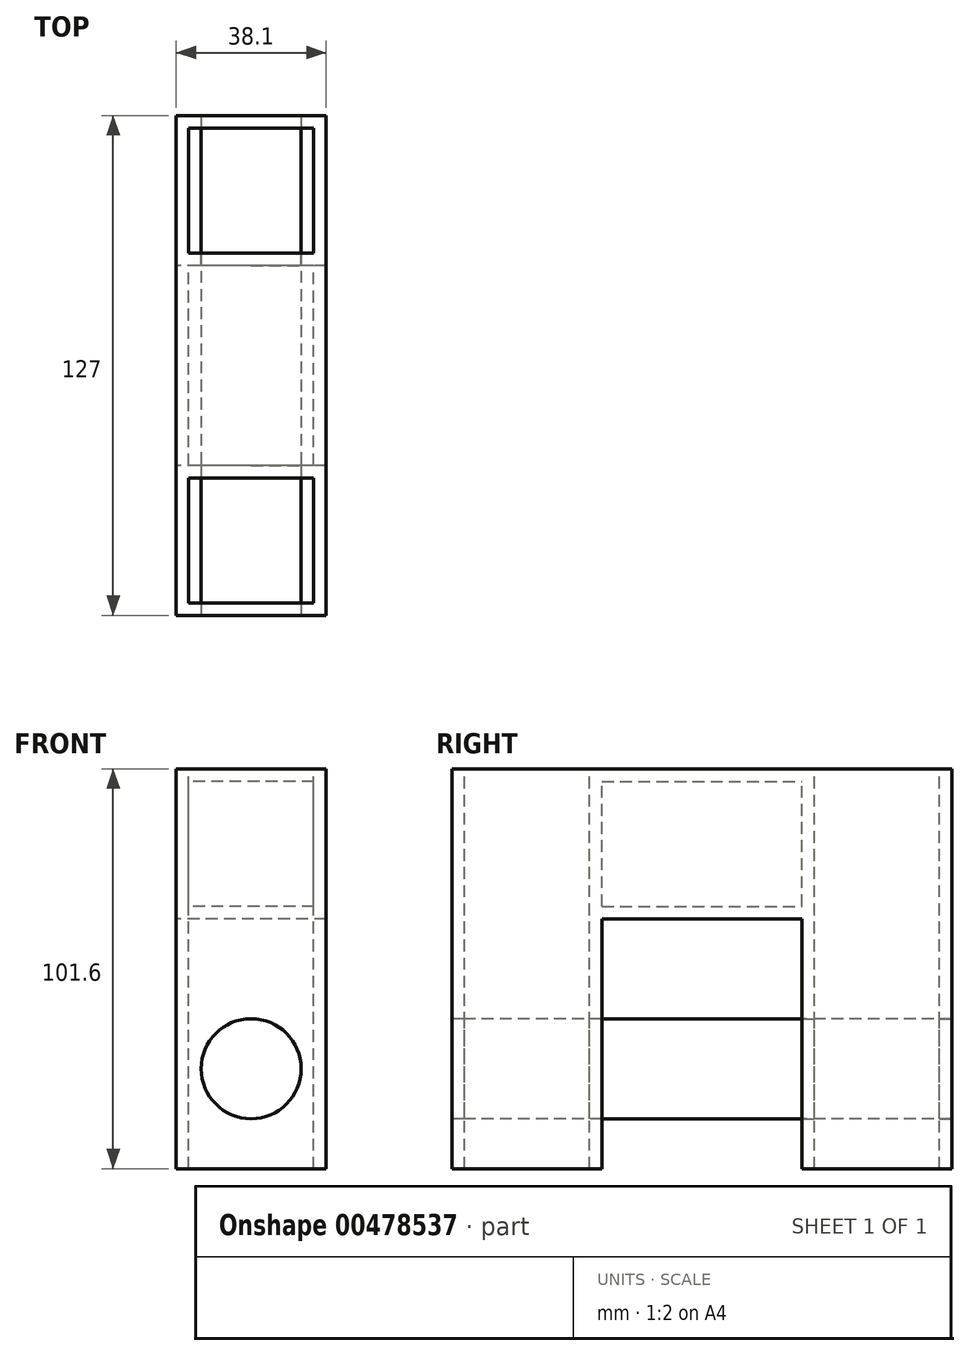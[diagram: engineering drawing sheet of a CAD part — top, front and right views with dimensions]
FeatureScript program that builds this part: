
annotation { "Feature Type Name" : "Feature", "Feature Type Description" : "" }
export const myFeature = defineFeature(function(context is Context, id is Id, definition is map)
    precondition{}
    {
        {
            var Q0;
            Q0=qCreatedBy(makeId("Front.planeOp"),FACE);
            var sketch = newSketch(context, id + "F0", { "sketchPlane" : qUnion([Q0])});
            skLineSegment(sketch, "E0.bottom", {"start": v(0, 0) * mm, "end": v(-38.1, 0) * mm});
            skLineSegment(sketch, "E0.top", {"start": v(0, 38.1) * mm, "end": v(-38.1, 38.1) * mm});
            skLineSegment(sketch, "E0.left", {"start": v(0, 0) * mm, "end": v(0, 38.1) * mm});
            skLineSegment(sketch, "E0.right", {"start": v(-38.1, 0) * mm, "end": v(-38.1, 38.1) * mm});
            skLineSegment(sketch, "E1.0", {"start": v(-34.92, 3.17) * mm, "end": v(-34.92, 34.93) * mm});
            skLineSegment(sketch, "E1.1", {"start": v(-3.17, 3.17) * mm, "end": v(-34.92, 3.17) * mm});
            skLineSegment(sketch, "E1.2", {"start": v(-3.17, 3.17) * mm, "end": v(-3.17, 34.93) * mm});
            skLineSegment(sketch, "E1.3", {"start": v(-3.17, 34.93) * mm, "end": v(-34.92, 34.93) * mm});
            skSolve(sketch);
        }
        {
            var Q0;
            Q0=makeQuery(id+"F0.imprint","IMPRINT",FACE,{"disambiguationData":[TD([[makeQuery(id+"F0.imprint","IMPRINT",EDGE,{"derivedFrom":sQuery(id+"F0.wireOp",EDGE,"E0.bottom")}),-1.0]])]});
            extrude(context, id + "F1", {"entities" : qUnion([Q0]), "depth" : 50.8 * mm});
        }
        {
            var Q0;
            Q0=makeQuery(id+"F1.opExtrude","SWEPT_FACE",FACE,{"disambiguationData":[OSD([sQuery(id+"F0.wireOp",EDGE,"E0.top")])]});
            var sketch = newSketch(context, id + "F2", { "sketchPlane" : qUnion([Q0])});
            skLineSegment(sketch, "E2.bottom", {"start": v(-38.1, -50.8) * mm, "end": v(0, -50.8) * mm});
            skLineSegment(sketch, "E2.top", {"start": v(-38.1, -88.9) * mm, "end": v(0, -88.9) * mm});
            skLineSegment(sketch, "E2.left", {"start": v(-38.1, -50.8) * mm, "end": v(-38.1, -88.9) * mm});
            skLineSegment(sketch, "E2.right", {"start": v(0, -50.8) * mm, "end": v(0, -88.9) * mm});
            skLineSegment(sketch, "E3.0", {"start": v(-34.92, -53.98) * mm, "end": v(-34.92, -85.73) * mm});
            skLineSegment(sketch, "E3.1", {"start": v(-34.92, -53.98) * mm, "end": v(-3.17, -53.98) * mm});
            skLineSegment(sketch, "E3.2", {"start": v(-3.17, -53.98) * mm, "end": v(-3.17, -85.73) * mm});
            skLineSegment(sketch, "E3.3", {"start": v(-34.92, -85.73) * mm, "end": v(-3.17, -85.73) * mm});
            skSolve(sketch);
        }
        {
            var Q0;
            Q0=makeQuery(id+"F2.imprint","IMPRINT",FACE,{"disambiguationData":[TD([[makeQuery(id+"F2.imprint","IMPRINT",EDGE,{"derivedFrom":sQuery(id+"F2.wireOp",EDGE,"E2.bottom")}),1.0]])]});
            extrude(context, id + "F3", {"entities" : qUnion([Q0]), "oppositeDirection" : true, "depth" : 101.6 * mm});
        }
        {
            var Q0;
            Q0=makeQuery(id+"F1.opExtrude","CAP_FACE",FACE,{"disambiguationData":[OSD([sQuery(id+"F0.wireOp",EDGE,"E0.bottom"),sQuery(id+"F0.wireOp",EDGE,"E0.top"),sQuery(id+"F0.wireOp",EDGE,"E0.left"),sQuery(id+"F0.wireOp",EDGE,"E0.right"),sQuery(id+"F0.wireOp",EDGE,"E1.0"),sQuery(id+"F0.wireOp",EDGE,"E1.1"),sQuery(id+"F0.wireOp",EDGE,"E1.2"),sQuery(id+"F0.wireOp",EDGE,"E1.3")])],"isStart":true});
            cPlane(context, id + "F4", {"entities" : qUnion([Q0]), "cplaneType" : CPlaneType.OFFSET, "offset" : 25.4 * mm, "oppositeDirection" : true, "width" : 152.4 * mm, "height" : 152.4 * mm});
        }
        {
            var Q0;
            Q0=makeQuery(id+"F3.opExtrude","SWEPT_FACE",FACE,{"disambiguationData":[OSD([sQuery(id+"F2.wireOp",EDGE,"E2.top")])]});
            var sketch = newSketch(context, id + "F5", { "sketchPlane" : qUnion([Q0])});
            skCircle(sketch, "E4", {"center": v(-19.05, -38.1) * mm, "radius": 12.7 * mm});
            skPoint(sketch, "E4.centerSnap0", {"position": v(-19.05, -63.5) * mm});
            skSolve(sketch);
        }
        {
            var Q0;
            Q0=makeQuery(id+"F5.imprint","IMPRINT",FACE,{"disambiguationData":[TD([[makeQuery(id+"F5.imprint","IMPRINT",EDGE,{"derivedFrom":sQuery(id+"F5.wireOp",EDGE,"E4")}),1.0]])]});
            extrude(context, id + "F6", {"entities" : qUnion([Q0]), "operationType" : NewBodyOperationType.REMOVE, "endBound" : BoundingType.THROUGH_ALL, "oppositeDirection" : true, "depth" : 25.4 * mm});
        }
        {
            var Q0;
            Q0=makeQuery(id+"F3.opExtrude","SWEPT_BODY",BODY,{"disambiguationData":[OSD([sQuery(id+"F2.wireOp",EDGE,"E2.bottom"),sQuery(id+"F2.wireOp",EDGE,"E2.top"),sQuery(id+"F2.wireOp",EDGE,"E2.left"),sQuery(id+"F2.wireOp",EDGE,"E2.right"),sQuery(id+"F2.wireOp",EDGE,"E3.0"),sQuery(id+"F2.wireOp",EDGE,"E3.1"),sQuery(id+"F2.wireOp",EDGE,"E3.2"),sQuery(id+"F2.wireOp",EDGE,"E3.3")])]});
            var Q1;
            Q1=qCreatedBy(id+"F4.planeOp",FACE);
            mirror(context, id + "F7", {"operationType" : NewBodyOperationType.ADD, "entities" : qUnion([Q0]), "mirrorPlane" : qUnion([Q1])});
        }
        {
            var Q0;
            Q0=makeQuery(id+"F3.opExtrude","SWEPT_FACE",FACE,{"disambiguationData":[OSD([sQuery(id+"F2.wireOp",EDGE,"E2.top")])]});
            var sketch = newSketch(context, id + "F8", { "sketchPlane" : qUnion([Q0])});
            skCircle(sketch, "E5", {"center": v(-19.05, -38.1) * mm, "radius": 12.7 * mm});
            skSolve(sketch);
        }
        {
            var Q0;
            Q0=makeQuery(id+"F8.imprint","IMPRINT",FACE,{"disambiguationData":[TD([[makeQuery(id+"F8.imprint","IMPRINT",EDGE,{"derivedFrom":sQuery(id+"F8.wireOp",EDGE,"E5")}),1.0]])]});
            extrude(context, id + "F9", {"entities" : qUnion([Q0]), "oppositeDirection" : true, "depth" : 127 * mm});
        }
    });
